# Revit family: Sink-Kitchen-KOHLER-Kennon-K-8437
name_source: partatom
category: Plumbing Fixtures
revit_build: Autodesk Revit 2015 (Build: 20140606_1530(x64)
units: mm (PartAtom-declared; Revit-internal decimal feet)

## types (2) — shared parameters
ADA Compliant = No
Assembly Code = D2010400
CW Connection = No
Cold Water Inlet = Cold Water Inlet
Date Modified = 04/25/2018
Default Elevation = 36"
Description = 33inch x 22inch x 10-1/8inch Neoroc top-/under-mount single-bowl kitchen sink
HW Connection = No
Height = 10 1/8"
Hot Water Inlet = Hot Water Inlet
Length = 33"
Manufacturer = KOHLER Co.
MasterFormat 1995 = 15410
MasterFormat 2004 = 22.41.16
Material = Neoroc
Product Documentation Link = http://www.us.kohler.com
Product Name = Kennon
Product Page URL = http://www.us.kohler.com
URL = https://www.us.kohler.com
Vent Connection = No
Waste Connection = Yes
Waste Water Outlet = Waste Water Outlet
Width = 22"

## per-type parameters (varying)
| type | Finish | Model | Type |
| CM1- Neoroc Matte Black | Kohler-Neoroc-CM1-Matte_Black | K-8437-1-CM1 | 1 |
| CM2- Neoroc Matte Brown | Kohler-Neoroc-CM2-Matte_Brown | K-8437-1-CM2 | 2 |

## geometry (parser evidence)
native form markers: Sweep x6
no freeform markers — native parametric forms only
